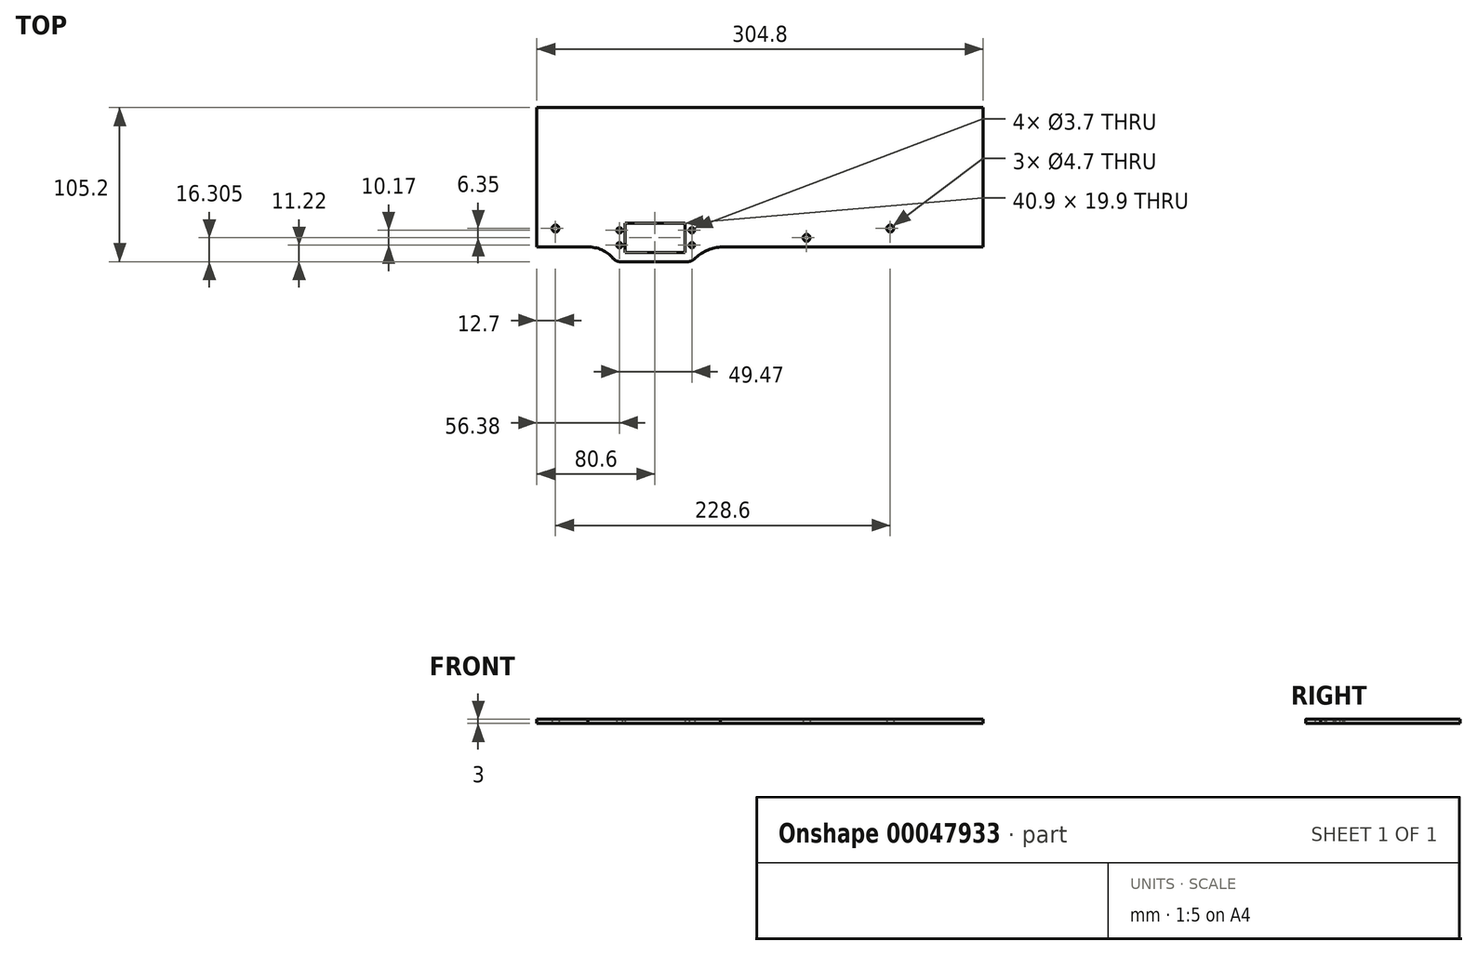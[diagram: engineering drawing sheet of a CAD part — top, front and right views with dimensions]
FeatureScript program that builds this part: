
annotation { "Feature Type Name" : "Feature", "Feature Type Description" : "" }
export const myFeature = defineFeature(function(context is Context, id is Id, definition is map)
    precondition{}
    {
        {
            var Q0;
            Q0=qCreatedBy(makeId("Top.planeOp"),FACE);
            var sketch = newSketch(context, id + "F0", { "sketchPlane" : qUnion([Q0])});
            skLineSegment(sketch, "E0.rect.bottom", {"start": v(-152.4, -47.63) * mm, "end": v(-116.13, -47.63) * mm});
            skLineSegment(sketch, "E0.rect.top", {"start": v(-152.4, 47.63) * mm, "end": v(152.4, 47.63) * mm});
            skLineSegment(sketch, "E0.rect.left", {"start": v(-152.4, -47.63) * mm, "end": v(-152.4, 47.63) * mm});
            skLineSegment(sketch, "E0.rect.right", {"start": v(152.4, -47.63) * mm, "end": v(152.4, 47.63) * mm});
            skPoint(sketch, "E0.rect.middle", {"position": v(0, 0) * mm});
            skPoint(sketch, "E1.endSnap0", {"position": v(0, -47.63) * mm});
            skLineSegment(sketch, "E2", {"start": v(-152.4, -34.92) * mm, "end": v(-139.7, -34.92) * mm, "construction": true});
            skCircle(sketch, "E3", {"center": v(-139.7, -34.92) * mm, "radius": 2.35 * mm});
            skLineSegment(sketch, "E4.bottom", {"start": v(152.4, -47.62) * mm, "end": v(101.6, -47.63) * mm, "construction": true});
            skLineSegment(sketch, "E4.top", {"start": v(152.4, 0) * mm, "end": v(101.6, 0) * mm, "construction": true});
            skLineSegment(sketch, "E4.left", {"start": v(152.4, -47.63) * mm, "end": v(152.4, 0) * mm, "construction": true});
            skLineSegment(sketch, "E4.right", {"start": v(101.6, -47.63) * mm, "end": v(101.6, 0) * mm, "construction": true});
            skLineSegment(sketch, "E5", {"start": v(101.6, -34.92) * mm, "end": v(88.9, -34.92) * mm, "construction": true});
            skCircle(sketch, "E6", {"center": v(88.9, -34.92) * mm, "radius": 2.35 * mm});
            skLineSegment(sketch, "E7", {"start": v(-139.7, -34.92) * mm, "end": v(88.9, -34.92) * mm, "construction": true});
            skLineSegment(sketch, "E8", {"start": v(-25.4, -34.92) * mm, "end": v(-25.4, -47.63) * mm, "construction": true});
            skPoint(sketch, "E9.endSnap0", {"position": v(-25.4, -41.27) * mm});
            skPoint(sketch, "E10.endSnap0", {"position": v(0, 47.63) * mm});
            skLineSegment(sketch, "E11", {"start": v(0, 47.63) * mm, "end": v(0, 41.28) * mm, "construction": true});
            skLineSegment(sketch, "E12", {"start": v(0, 41.28) * mm, "end": v(-152.4, 41.28) * mm, "construction": true});
            skLineSegment(sketch, "E13", {"start": v(0, 41.28) * mm, "end": v(152.4, 41.28) * mm, "construction": true});
            skCircle(sketch, "E14", {"center": v(31.75, -41.27) * mm, "radius": 2.35 * mm});
            skLineSegment(sketch, "E15", {"start": v(-96.02, -41.27) * mm, "end": v(-96.02, -36.19) * mm, "construction": true});
            skLineSegment(sketch, "E16", {"start": v(-96.02, -41.27) * mm, "end": v(-96.02, -46.36) * mm, "construction": true});
            skLineSegment(sketch, "E17", {"start": v(-82.55, -41.27) * mm, "end": v(-46.55, -41.27) * mm, "construction": true});
            skLineSegment(sketch, "E18", {"start": v(-82.55, -41.27) * mm, "end": v(-92.25, -41.27) * mm, "construction": true});
            skLineSegment(sketch, "E19", {"start": v(-82.55, -41.27) * mm, "end": v(-25.4, -41.27) * mm, "construction": true});
            skLineSegment(sketch, "E20", {"start": v(-92.25, -41.27) * mm, "end": v(-92.25, -31.32) * mm, "construction": true});
            skLineSegment(sketch, "E21", {"start": v(-92.25, -31.32) * mm, "end": v(-51.35, -31.32) * mm, "construction": true});
            skLineSegment(sketch, "E22.bottom", {"start": v(-92.25, -31.32) * mm, "end": v(-51.35, -31.32) * mm});
            skLineSegment(sketch, "E22.top", {"start": v(-92.25, -51.23) * mm, "end": v(-51.35, -51.23) * mm});
            skLineSegment(sketch, "E22.left", {"start": v(-92.25, -31.32) * mm, "end": v(-92.25, -51.23) * mm});
            skLineSegment(sketch, "E22.right", {"start": v(-51.35, -31.32) * mm, "end": v(-51.35, -51.22) * mm});
            skLineSegment(sketch, "E23", {"start": v(-77.1, -57.57) * mm, "end": v(-95.5, -57.57) * mm});
            skArc(sketch, "E24", {"start": v(-100.37, -55.32) * mm, "mid": v(-108.16, -49.47) * mm, "end": v(-117.73, -47.63) * mm});
            skPoint(sketch, "E25.visualSharp", {"position": v(-98.7, -57.57) * mm});
            skArc(sketch, "E25.filletArc", {"start": v(-100.37, -55.32) * mm, "mid": v(-98.19, -56.98) * mm, "end": v(-95.5, -57.57) * mm});
            skCircle(sketch, "E26", {"center": v(-96.02, -36.19) * mm, "radius": 1.85 * mm});
            skCircle(sketch, "E27", {"center": v(-96.02, -46.36) * mm, "radius": 1.85 * mm});
            skCircle(sketch, "E28", {"center": v(-46.55, -36.19) * mm, "radius": 1.85 * mm});
            skLineSegment(sketch, "E29.trimOffspring", {"start": v(-27.11, -47.63) * mm, "end": v(152.4, -47.63) * mm});
            skCircle(sketch, "E30", {"center": v(-46.55, -46.36) * mm, "radius": 1.85 * mm});
            skCircle(sketch, "E31", {"center": v(-82.55, -41.27) * mm, "radius": 5 * mm, "construction": true});
            skLineSegment(sketch, "E32", {"start": v(-77.1, -57.57) * mm, "end": v(-49.42, -57.57) * mm});
            skArc(sketch, "E33", {"start": v(-27.11, -47.63) * mm, "mid": v(-36.75, -50.06) * mm, "end": v(-44.93, -55.72) * mm});
            skPoint(sketch, "E34.visualSharp", {"position": v(-46.63, -57.58) * mm});
            skArc(sketch, "E34.filletArc", {"start": v(-49.42, -57.57) * mm, "mid": v(-46.99, -57.1) * mm, "end": v(-44.93, -55.72) * mm});
            skSolve(sketch);
        }
        {
            var Q0;
            Q0=makeQuery(id+"F0.imprint","IMPRINT",FACE,{"disambiguationData":[TD([[makeQuery(id+"F0.imprint","IMPRINT",EDGE,{"derivedFrom":sQuery(id+"F0.wireOp",EDGE,"E0.rect.top")}),-1.0]])]});
            extrude(context, id + "F1", {"entities" : qUnion([Q0]), "depth" : 3 * mm});
        }
    });
